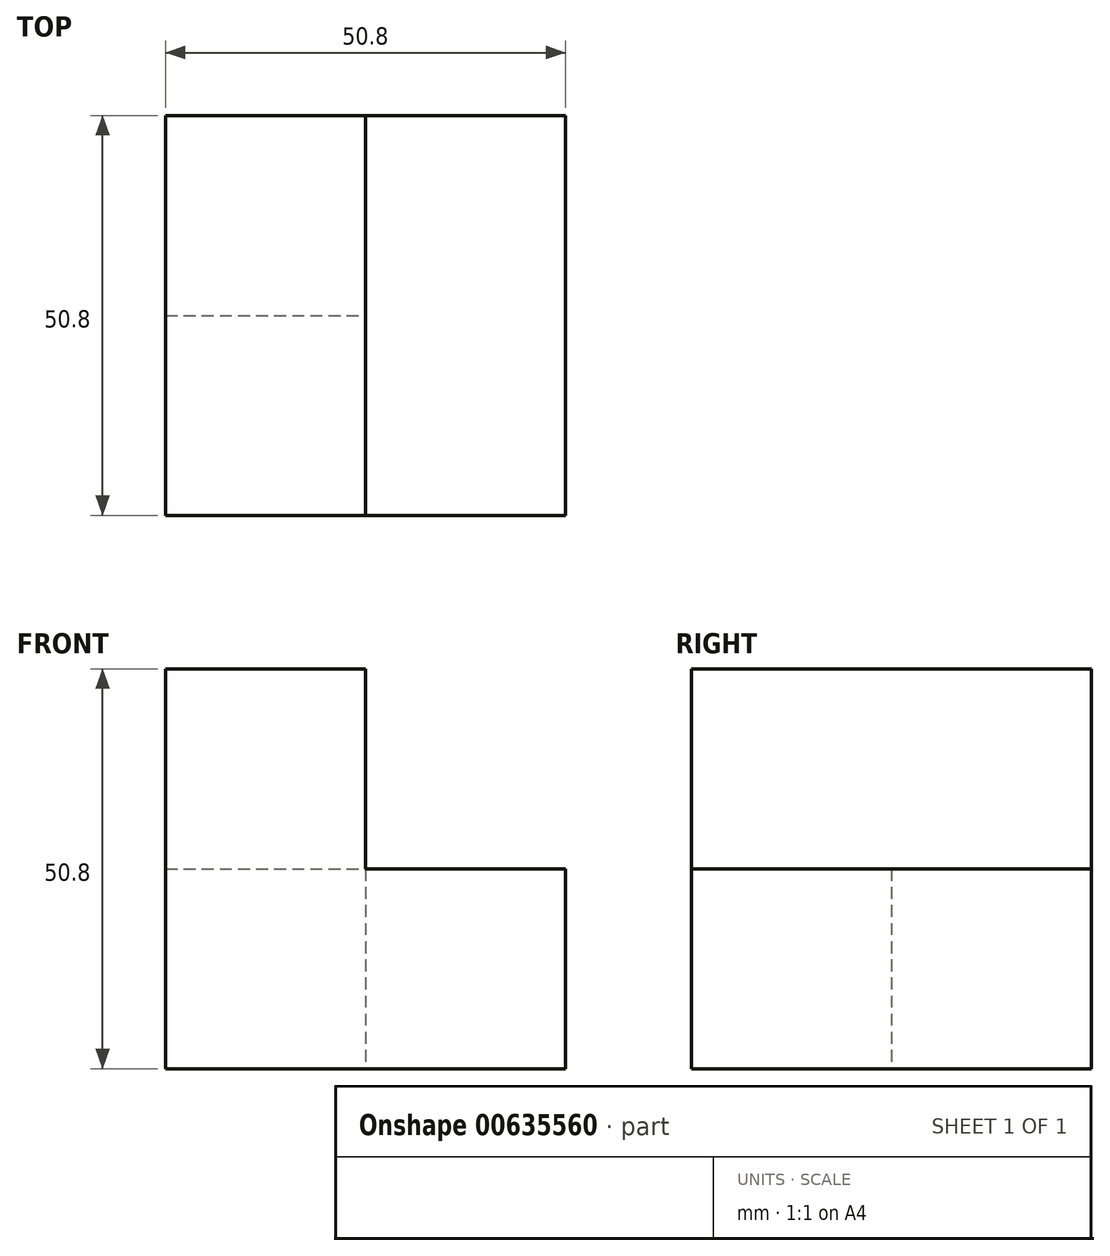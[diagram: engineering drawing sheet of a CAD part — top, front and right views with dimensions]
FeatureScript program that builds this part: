
annotation { "Feature Type Name" : "Feature", "Feature Type Description" : "" }
export const myFeature = defineFeature(function(context is Context, id is Id, definition is map)
    precondition{}
    {
        {
            var Q0;
            Q0=qCreatedBy(makeId("Top.planeOp"),FACE);
            var sketch = newSketch(context, id + "F0", { "sketchPlane" : qUnion([Q0])});
            skLineSegment(sketch, "E0.bottom", {"start": v(0, 0) * mm, "end": v(25.4, 0) * mm});
            skLineSegment(sketch, "E0.top", {"start": v(0, 25.4) * mm, "end": v(25.4, 25.4) * mm});
            skLineSegment(sketch, "E0.left", {"start": v(0, 0) * mm, "end": v(0, 25.4) * mm});
            skLineSegment(sketch, "E0.right", {"start": v(25.4, 0) * mm, "end": v(25.4, 25.4) * mm});
            skLineSegment(sketch, "E1.top", {"start": v(0, 50.8) * mm, "end": v(25.4, 50.8) * mm});
            skLineSegment(sketch, "E1.left", {"start": v(0, 0) * mm, "end": v(0, 50.8) * mm});
            skLineSegment(sketch, "E1.right", {"start": v(25.4, 0) * mm, "end": v(25.4, 50.8) * mm});
            skLineSegment(sketch, "E2.bottom", {"start": v(25.4, 0) * mm, "end": v(50.8, 0) * mm});
            skLineSegment(sketch, "E2.top", {"start": v(25.4, 50.8) * mm, "end": v(50.8, 50.8) * mm});
            skLineSegment(sketch, "E2.right", {"start": v(50.8, 0) * mm, "end": v(50.8, 50.8) * mm});
            skSolve(sketch);
        }
        {
            var Q0;
            {var subQ0=sQuery(id+"F0.wireOp",EDGE,"E0.top");Q0=makeQuery(id+"F0.imprint","IMPRINT",FACE,{"disambiguationData":[TD([[makeQuery(id+"F0.imprint","IMPRINT",EDGE,{"derivedFrom":subQ0}),-1.0]])]});}
            var Q1;
            {var subQ3=sQuery(id+"F0.wireOp",EDGE,"E2.bottom");Q1=makeQuery(id+"F0.imprint","IMPRINT",FACE,{"disambiguationData":[TD([[makeQuery(id+"F0.imprint","IMPRINT",EDGE,{"derivedFrom":subQ3}),1.0]])]});}
            var Q2;
            {var subQ0=sQuery(id+"F0.wireOp",EDGE,"E0.top");Q2=makeQuery(id+"F0.imprint","IMPRINT",FACE,{"disambiguationData":[TD([[makeQuery(id+"F0.imprint","IMPRINT",EDGE,{"derivedFrom":subQ0}),1.0]])]});}
            extrude(context, id + "F1", {"entities" : qUnion([Q0, Q1, Q2]), "depth" : 25.4 * mm, "offsetDistance" : 25.4 * mm});
        }
        {
            var Q0;
            {var subQ0=sQuery(id+"F0.wireOp",EDGE,"E0.top");Q0=makeQuery(id+"F0.imprint","IMPRINT",FACE,{"disambiguationData":[TD([[makeQuery(id+"F0.imprint","IMPRINT",EDGE,{"derivedFrom":subQ0}),1.0]])]});}
            var Q1;
            {var subQ0=sQuery(id+"F0.wireOp",EDGE,"E0.top");Q1=makeQuery(id+"F0.imprint","IMPRINT",FACE,{"disambiguationData":[TD([[makeQuery(id+"F0.imprint","IMPRINT",EDGE,{"derivedFrom":subQ0}),-1.0]])]});}
            extrude(context, id + "F2", {"entities" : qUnion([Q0, Q1]), "operationType" : NewBodyOperationType.ADD, "depth" : 50.8 * mm, "offsetDistance" : 25.4 * mm});
        }
        {
            var Q0;
            {var subQ0=sQuery(id+"F0.wireOp",EDGE,"E0.top");Q0=makeQuery(id+"F0.imprint","IMPRINT",FACE,{"disambiguationData":[TD([[makeQuery(id+"F0.imprint","IMPRINT",EDGE,{"derivedFrom":subQ0}),1.0]])]});}
            extrude(context, id + "F3", {"entities" : qUnion([Q0]), "operationType" : NewBodyOperationType.REMOVE, "depth" : 25.37 * mm, "offsetDistance" : 25.4 * mm});
        }
    });
